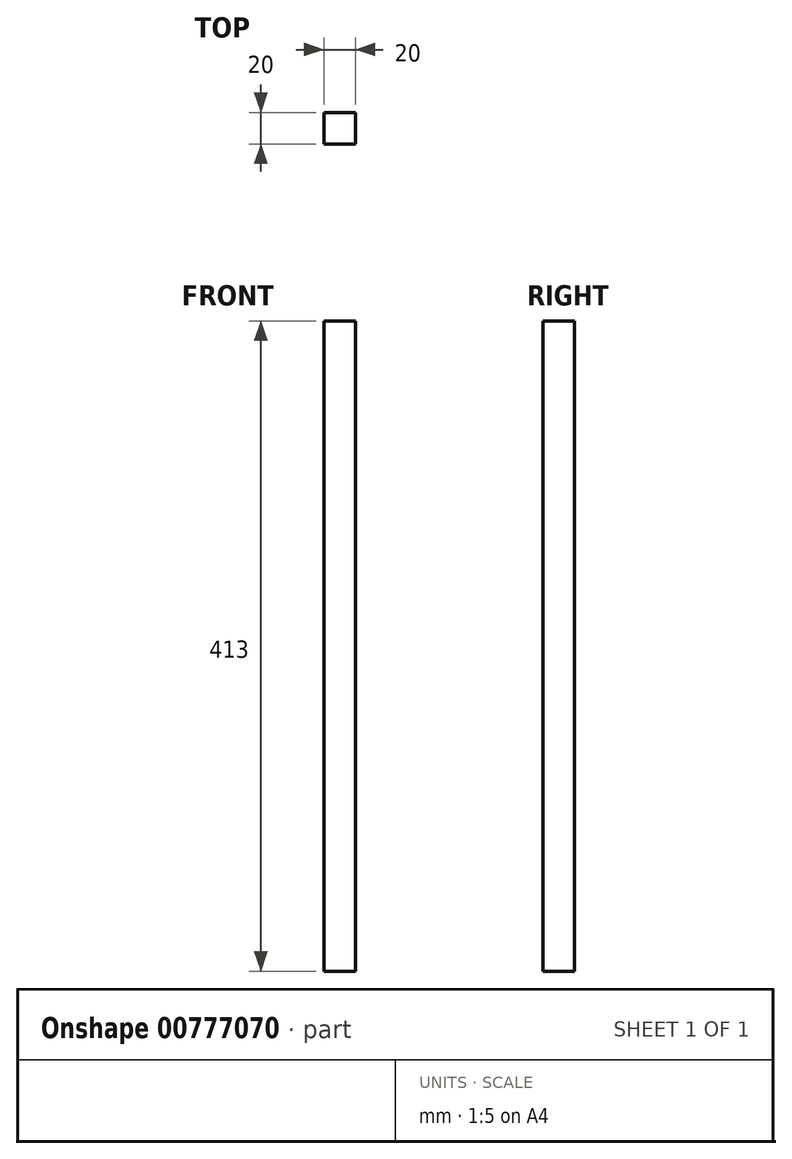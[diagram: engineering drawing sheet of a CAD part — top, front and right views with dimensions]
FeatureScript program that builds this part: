
annotation { "Feature Type Name" : "Feature", "Feature Type Description" : "" }
export const myFeature = defineFeature(function(context is Context, id is Id, definition is map)
    precondition{}
    {
        {
            var Q0;
            Q0=qCreatedBy(makeId("Top.planeOp"),FACE);
            var sketch = newSketch(context, id + "F0", { "sketchPlane" : qUnion([Q0])});
            skLineSegment(sketch, "E0.bottom", {"start": v(-10, 10) * mm, "end": v(10, 10) * mm});
            skLineSegment(sketch, "E0.top", {"start": v(-10, -10) * mm, "end": v(10, -10) * mm});
            skLineSegment(sketch, "E0.left", {"start": v(-10, 10) * mm, "end": v(-10, -10) * mm});
            skLineSegment(sketch, "E0.right", {"start": v(10, 10) * mm, "end": v(10, -10) * mm});
            skSolve(sketch);
        }
        {
            var Q0;
            Q0=qSketchRegion(id+"F0",true);
            extrude(context, id + "F1", {"entities" : qUnion([Q0]), "depth" : (492 - 79) * mm, "offsetDistance" : 25 * mm});
        }
    });
